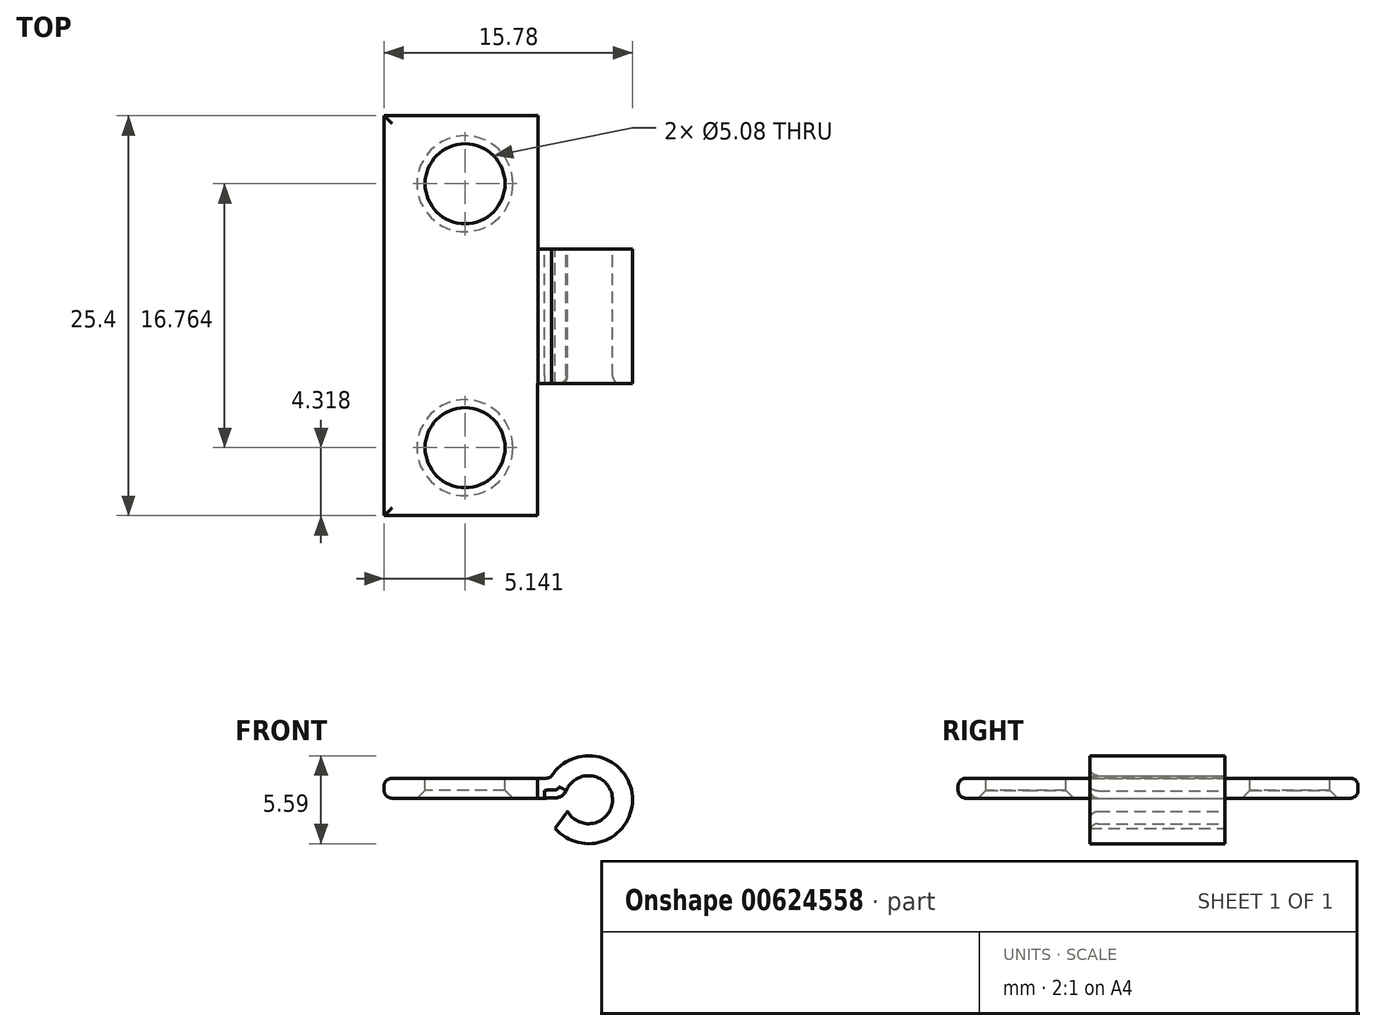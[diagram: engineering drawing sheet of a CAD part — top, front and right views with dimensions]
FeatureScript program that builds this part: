
annotation { "Feature Type Name" : "Feature", "Feature Type Description" : "" }
export const myFeature = defineFeature(function(context is Context, id is Id, definition is map)
    precondition{}
    {
        {
            var Q0;
            Q0=qCreatedBy(makeId("Front.planeOp"),FACE);
            var sketch = newSketch(context, id + "F0", { "sketchPlane" : qUnion([Q0])});
            skLineSegment(sketch, "E0.bottom", {"start": v(-28.78, 12.85) * mm, "end": v(-19, 12.85) * mm});
            skLineSegment(sketch, "E0.top", {"start": v(-28.78, 11.58) * mm, "end": v(-18.59, 11.58) * mm});
            skLineSegment(sketch, "E0.left", {"start": v(-28.78, 12.85) * mm, "end": v(-28.78, 11.58) * mm});
            skArc(sketch, "E1", {"start": v(-17.91, 9.66) * mm, "mid": v(-13, 11.69) * mm, "end": v(-18.15, 12.99) * mm});
            skPoint(sketch, "E1.centerSnap0", {"position": v(-18.61, 11.49) * mm});
            skArc(sketch, "E2", {"start": v(-17.13, 10.75) * mm, "mid": v(-14.27, 11.59) * mm, "end": v(-17.21, 12.05) * mm});
            skFitSpline(sketch, "E3", {"points": [v(-17.21, 12.05) * mm, v(-17.65, 11.65) * mm, v(-18.59, 11.58) * mm], "startDerivative": vector(-1.12, -1.46) * mm, "endDerivative": vector(-2.02, -0.1) * mm});
            skLineSegment(sketch, "E4", {"start": v(-17.13, 10.75) * mm, "end": v(-17.91, 9.66) * mm});
            skFitSpline(sketch, "E5", {"points": [v(-19, 12.85) * mm, v(-18.59, 12.85) * mm, v(-18.15, 12.99) * mm], "startDerivative": vector(0.67, 0) * mm, "endDerivative": vector(0.6, 0.75) * mm});
            skSolve(sketch);
        }
        {
            var Q0;
            Q0=qSketchRegion(id+"F0",true);
            extrude(context, id + "F1", {"entities" : qUnion([Q0]), "depth" : 25.4 * mm});
        }
        {
            var Q0;
            Q0=makeQuery(id+"F1.opExtrude","SWEPT_FACE",FACE,{"disambiguationData":[OSD([sQuery(id+"F0.wireOp",EDGE,"E0.bottom")])]});
            var sketch = newSketch(context, id + "F2", { "sketchPlane" : qUnion([Q0])});
            skLineSegment(sketch, "E6.bottom", {"start": v(-19.02, -17.02) * mm, "end": v(-10.92, -17.02) * mm});
            skLineSegment(sketch, "E6.top", {"start": v(-19.02, -25.4) * mm, "end": v(-10.92, -25.4) * mm});
            skLineSegment(sketch, "E6.left", {"start": v(-19.02, -17.02) * mm, "end": v(-19.02, -25.4) * mm});
            skLineSegment(sketch, "E6.right", {"start": v(-10.92, -17.02) * mm, "end": v(-10.92, -25.4) * mm});
            skLineSegment(sketch, "E7.bottom", {"start": v(-19, 0) * mm, "end": v(-9.4, 0) * mm});
            skLineSegment(sketch, "E7.top", {"start": v(-19, -8.46) * mm, "end": v(-9.4, -8.46) * mm});
            skLineSegment(sketch, "E7.left", {"start": v(-19, 0) * mm, "end": v(-19, -8.46) * mm});
            skLineSegment(sketch, "E7.right", {"start": v(-9.4, 0) * mm, "end": v(-9.4, -8.46) * mm});
            skSolve(sketch);
        }
        {
            var Q0;
            Q0=qSketchRegion(id+"F2",true);
            extrude(context, id + "F3", {"entities" : qUnion([Q0]), "operationType" : NewBodyOperationType.REMOVE, "endBound" : BoundingType.SYMMETRIC, "oppositeDirection" : true, "depth" : 25.4 * mm});
        }
        {
            var Q0;
            Q0=makeQuery(id+"F1.opExtrude","CAP_EDGE",EDGE,{"disambiguationData":[OSD([sQuery(id+"F0.wireOp",EDGE,"E0.bottom")])],"isStart":false});
            var Q1;
            Q1=makeQuery(id+"F1.opExtrude","SWEPT_EDGE",EDGE,{"disambiguationData":[OSD([sQuery(id+"F0.wireOp",EDGE,"E0.bottom"),sQuery(id+"F0.wireOp",EDGE,"E0.left")])]});
            var Q2;
            Q2=makeQuery(id+"F1.opExtrude","CAP_EDGE",EDGE,{"disambiguationData":[OSD([sQuery(id+"F0.wireOp",EDGE,"E0.bottom")])],"isStart":true});
            var Q3;
            Q3=makeQuery(id+"F1.opExtrude","CAP_EDGE",EDGE,{"disambiguationData":[OSD([sQuery(id+"F0.wireOp",EDGE,"E0.top")])],"isStart":false});
            var Q4;
            Q4=makeQuery(id+"F1.opExtrude","SWEPT_EDGE",EDGE,{"disambiguationData":[OSD([sQuery(id+"F0.wireOp",EDGE,"E0.top"),sQuery(id+"F0.wireOp",EDGE,"E0.left")])]});
            var Q5;
            Q5=makeQuery(id+"F1.opExtrude","CAP_EDGE",EDGE,{"disambiguationData":[OSD([sQuery(id+"F0.wireOp",EDGE,"E0.top")])],"isStart":true});
            var Q6;
            Q6=makeQuery(id+"F3.boolean.opBoolean","INTERSECT",EDGE,{"derivedFrom":[makeQuery(id+"F1.opExtrude","SWEPT_FACE",FACE,{"disambiguationData":[OSD([sQuery(id+"F0.wireOp",EDGE,"E0.top")])]}),makeQuery(id+"F3.opExtrude","SWEPT_FACE",FACE,{"disambiguationData":[OSD([sQuery(id+"F2.wireOp",EDGE,"E6.top")])]})]});
            var Q7;
            Q7=makeQuery(id+"F3.boolean.opBoolean","INTERSECT",EDGE,{"derivedFrom":[makeQuery(id+"F1.opExtrude","SWEPT_FACE",FACE,{"disambiguationData":[OSD([sQuery(id+"F0.wireOp",EDGE,"E3")])]}),makeQuery(id+"F3.opExtrude","SWEPT_FACE",FACE,{"disambiguationData":[OSD([sQuery(id+"F2.wireOp",EDGE,"E6.bottom")])]})]});
            var Q8;
            Q8=makeQuery(id+"F3.boolean.opBoolean","INTERSECT",EDGE,{"derivedFrom":[makeQuery(id+"F1.opExtrude","SWEPT_FACE",FACE,{"disambiguationData":[OSD([sQuery(id+"F0.wireOp",EDGE,"E0.top")])]}),makeQuery(id+"F3.opExtrude","SWEPT_FACE",FACE,{"disambiguationData":[OSD([sQuery(id+"F2.wireOp",EDGE,"E6.bottom")])]})]});
            var Q9;
            Q9=makeQuery(id+"F3.boolean.opBoolean","INTERSECT",EDGE,{"derivedFrom":[makeQuery(id+"F1.opExtrude","SWEPT_FACE",FACE,{"disambiguationData":[OSD([sQuery(id+"F0.wireOp",EDGE,"E2")])]}),makeQuery(id+"F3.opExtrude","SWEPT_FACE",FACE,{"disambiguationData":[OSD([sQuery(id+"F2.wireOp",EDGE,"E6.bottom")])]})]});
            var Q10;
            Q10=makeQuery(id+"F3.boolean.opBoolean","INTERSECT",EDGE,{"derivedFrom":[makeQuery(id+"F1.opExtrude","SWEPT_FACE",FACE,{"disambiguationData":[OSD([sQuery(id+"F0.wireOp",EDGE,"E2")])]}),makeQuery(id+"F3.opExtrude","SWEPT_FACE",FACE,{"disambiguationData":[OSD([sQuery(id+"F2.wireOp",EDGE,"E6.top")])]})]});
            fillet(context, id + "F4", {"entities" : qUnion([Q0, Q1, Q2, Q3, Q4, Q5, Q6, Q7, Q8, Q9, Q10]), "radius" : 0.5 * mm, "tangentPropagation" : true, "allowEdgeOverflow" : false});
        }
        {
            var Q0;
            Q0=makeQuery(id+"F1.opExtrude","SWEPT_FACE",FACE,{"disambiguationData":[OSD([sQuery(id+"F0.wireOp",EDGE,"E0.bottom")])]});
            var sketch = newSketch(context, id + "F5", { "sketchPlane" : qUnion([Q0])});
            skCircle(sketch, "E8", {"center": v(-23.64, -4.32) * mm, "radius": 2.54 * mm});
            skPoint(sketch, "E8.centerSnap0", {"position": v(-23.64, -0.5) * mm});
            skCircle(sketch, "E9", {"center": v(-23.64, -21.08) * mm, "radius": 2.54 * mm});
            skSolve(sketch);
        }
        {
            var Q0;
            Q0=qSketchRegion(id+"F5",true);
            extrude(context, id + "F6", {"entities" : qUnion([Q0]), "operationType" : NewBodyOperationType.REMOVE, "oppositeDirection" : true, "depth" : 25.4 * mm});
        }
        {
            var Q0;
            Q0=makeQuery(id+"F6.boolean.opBoolean","COPY",EDGE,{"derivedFrom":makeQuery(id+"F6.opExtrude","CAP_EDGE",EDGE,{"disambiguationData":[OSD([sQuery(id+"F5.wireOp",EDGE,"E8")])],"isStart":true})});
            var Q1;
            Q1=makeQuery(id+"F6.boolean.opBoolean","INTERSECT",EDGE,{"derivedFrom":[makeQuery(id+"F1.opExtrude","SWEPT_FACE",FACE,{"disambiguationData":[OSD([sQuery(id+"F0.wireOp",EDGE,"E0.top")])]}),makeQuery(id+"F6.opExtrude","SWEPT_FACE",FACE,{"disambiguationData":[OSD([sQuery(id+"F5.wireOp",EDGE,"E8")])]})]});
            var Q2;
            Q2=makeQuery(id+"F6.boolean.opBoolean","COPY",EDGE,{"derivedFrom":makeQuery(id+"F6.opExtrude","CAP_EDGE",EDGE,{"disambiguationData":[OSD([sQuery(id+"F5.wireOp",EDGE,"E9")])],"isStart":true})});
            var Q3;
            Q3=makeQuery(id+"F6.boolean.opBoolean","INTERSECT",EDGE,{"derivedFrom":[makeQuery(id+"F1.opExtrude","SWEPT_FACE",FACE,{"disambiguationData":[OSD([sQuery(id+"F0.wireOp",EDGE,"E0.top")])]}),makeQuery(id+"F6.opExtrude","SWEPT_FACE",FACE,{"disambiguationData":[OSD([sQuery(id+"F5.wireOp",EDGE,"E9")])]})]});
            chamfer(context, id + "F7", {"entities" : qUnion([Q0, Q1, Q2, Q3]), "width" : 0.5 * mm, "tangentPropagation" : true});
        }
    });
